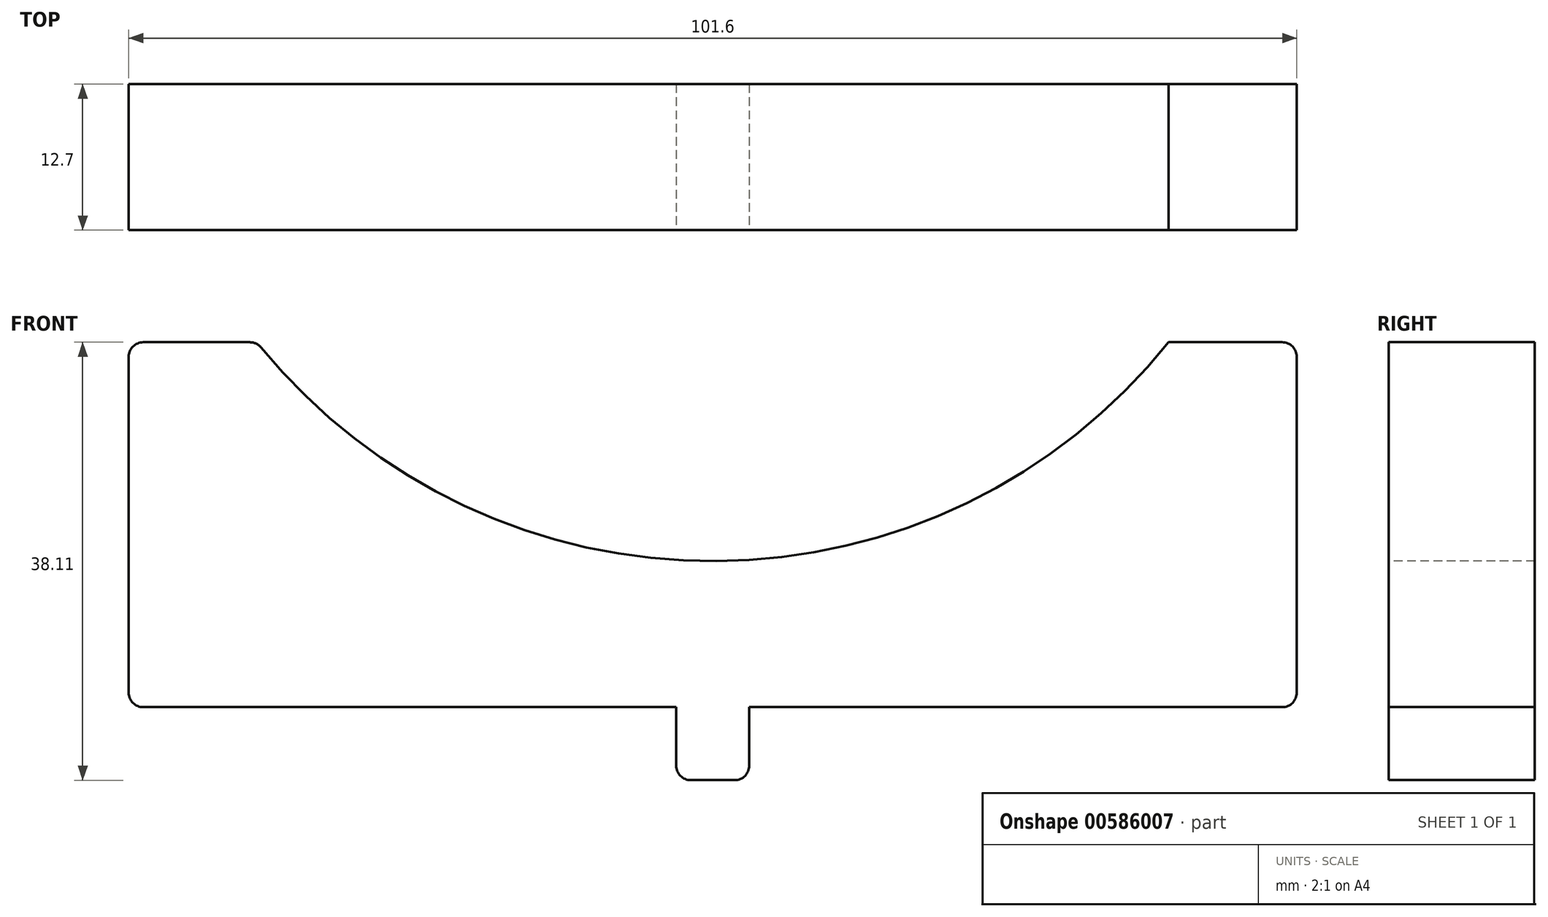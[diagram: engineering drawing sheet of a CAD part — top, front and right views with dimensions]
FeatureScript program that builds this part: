
annotation { "Feature Type Name" : "Feature", "Feature Type Description" : "" }
export const myFeature = defineFeature(function(context is Context, id is Id, definition is map)
    precondition{}
    {
        {
            var Q0;
            Q0=qCreatedBy(makeId("Front.planeOp"),FACE);
            var sketch = newSketch(context, id + "F0", { "sketchPlane" : qUnion([Q0])});
            skLineSegment(sketch, "E0.bottom", {"start": v(50.8, -15.87) * mm, "end": v(-50.8, -15.88) * mm});
            skLineSegment(sketch, "E0.top", {"start": v(50.8, 15.88) * mm, "end": v(-50.8, 15.87) * mm});
            skLineSegment(sketch, "E0.left", {"start": v(50.8, -15.88) * mm, "end": v(50.8, 15.88) * mm});
            skLineSegment(sketch, "E0.right", {"start": v(-50.8, -15.88) * mm, "end": v(-50.8, 15.87) * mm});
            skPoint(sketch, "E0.middle", {"position": v(0, 0) * mm});
            skSolve(sketch);
        }
        {
            var Q0;
            Q0=makeQuery(id+"F0.imprint","IMPRINT",FACE,{"disambiguationData":[TD([[makeQuery(id+"F0.imprint","IMPRINT",EDGE,{"derivedFrom":sQuery(id+"F0.wireOp",EDGE,"E0.bottom")}),-1.0]])]});
            extrude(context, id + "F1", {"entities" : qUnion([Q0]), "endBound" : BoundingType.SYMMETRIC, "depth" : 12.7 * mm, "offsetDistance" : 25.4 * mm});
        }
        {
            var Q0;
            Q0=qCreatedBy(makeId("Front.planeOp"),FACE);
            var sketch = newSketch(context, id + "F2", { "sketchPlane" : qUnion([Q0])});
            skArc(sketch, "E1", {"start": v(-39.66, 15.87) * mm, "mid": v(0, -3.17) * mm, "end": v(39.66, 15.87) * mm});
            skLineSegment(sketch, "E2", {"start": v(-39.66, 15.87) * mm, "end": v(39.66, 15.88) * mm});
            skSolve(sketch);
        }
        {
            var Q0;
            Q0 = qSketchRegion(id + "F2", true);
            extrude(context, id + "F3", {"entities" : qUnion([Q0]), "operationType" : NewBodyOperationType.REMOVE, "endBound" : BoundingType.SYMMETRIC, "oppositeDirection" : true, "depth" : 25.4 * mm, "offsetDistance" : 25.4 * mm});
        }
        {
            var Q0;
            Q0=makeQuery(id+"F1.opExtrude","SWEPT_FACE",FACE,{"disambiguationData":[OSD([sQuery(id+"F0.wireOp",EDGE,"E0.bottom")])]});
            var sketch = newSketch(context, id + "F4", { "sketchPlane" : qUnion([Q0])});
            skLineSegment(sketch, "E3.bottom", {"start": v(3.18, -6.35) * mm, "end": v(-3.18, -6.35) * mm});
            skLineSegment(sketch, "E3.top", {"start": v(3.18, 6.35) * mm, "end": v(-3.18, 6.35) * mm});
            skLineSegment(sketch, "E3.left", {"start": v(3.18, -6.35) * mm, "end": v(3.18, 6.35) * mm});
            skLineSegment(sketch, "E3.right", {"start": v(-3.18, -6.35) * mm, "end": v(-3.18, 6.35) * mm});
            skPoint(sketch, "E3.middle", {"position": v(0, 0) * mm});
            skSolve(sketch);
        }
        {
            var Q0;
            Q0=makeQuery(id+"F4.imprint","IMPRINT",FACE,{"disambiguationData":[TD([[makeQuery(id+"F4.imprint","IMPRINT",EDGE,{"derivedFrom":sQuery(id+"F4.wireOp",EDGE,"E3.bottom")}),-1.0]])]});
            extrude(context, id + "F5", {"entities" : qUnion([Q0]), "operationType" : NewBodyOperationType.ADD, "depth" : 6.35 * mm, "offsetDistance" : 25.4 * mm});
        }
        {
            var Q0;
            Q0=makeQuery(id+"F5.opExtrude","CAP_EDGE",EDGE,{"disambiguationData":[OSD([sQuery(id+"F4.wireOp",EDGE,"E3.right")])],"isStart":false});
            var Q1;
            Q1=makeQuery(id+"F5.opExtrude","CAP_EDGE",EDGE,{"disambiguationData":[OSD([sQuery(id+"F4.wireOp",EDGE,"E3.left")])],"isStart":false});
            var Q2;
            Q2=makeQuery(id+"F1.opExtrude","SWEPT_EDGE",EDGE,{"disambiguationData":[OSD([sQuery(id+"F0.wireOp",EDGE,"E0.bottom"),sQuery(id+"F0.wireOp",EDGE,"E0.right")])]});
            var Q3;
            Q3=makeQuery(id+"F1.opExtrude","SWEPT_EDGE",EDGE,{"disambiguationData":[OSD([sQuery(id+"F0.wireOp",EDGE,"E0.top"),sQuery(id+"F0.wireOp",EDGE,"E0.right")])]});
            var Q4;
            {var subQ0=sQuery(id+"F2.wireOp",EDGE,"E2");var subQ1=sQuery(id+"F2.wireOp",EDGE,"E1");Q4=makeQuery(id+"F3.boolean.opBoolean","COPY",EDGE,{"derivedFrom":makeQuery(id+"F3.opExtrude","SWEPT_EDGE",EDGE,{"disambiguationData":[OSD([subQ1,subQ0]),TDD([makeQuery(id+"F2.imprint","INTERSECT",VERTEX,{"disambiguationData":[OD(0.0)],"derivedFrom":[subQ1,subQ0]})])]})});}
            var Q5;
            {var subQ0=sQuery(id+"F2.wireOp",EDGE,"E2");var subQ1=sQuery(id+"F2.wireOp",EDGE,"E1");Q5=makeQuery(id+"F3.boolean.opBoolean","COPY",EDGE,{"derivedFrom":makeQuery(id+"F3.opExtrude","SWEPT_EDGE",EDGE,{"disambiguationData":[OSD([subQ1,subQ0]),TDD([makeQuery(id+"F2.imprint","INTERSECT",VERTEX,{"disambiguationData":[OD(1.0)],"derivedFrom":[subQ1,subQ0]})])]})});}
            var Q6;
            Q6=makeQuery(id+"F1.opExtrude","SWEPT_EDGE",EDGE,{"disambiguationData":[OSD([sQuery(id+"F0.wireOp",EDGE,"E0.top"),sQuery(id+"F0.wireOp",EDGE,"E0.left")])]});
            var Q7;
            Q7=makeQuery(id+"F1.opExtrude","SWEPT_EDGE",EDGE,{"disambiguationData":[OSD([sQuery(id+"F0.wireOp",EDGE,"E0.bottom"),sQuery(id+"F0.wireOp",EDGE,"E0.left")])]});
            fillet(context, id + "F6", {"entities" : qUnion([Q0, Q1, Q2, Q3, Q4, Q5, Q6, Q7]), "radius" : 1.27 * mm, "tangentPropagation" : true, "allowEdgeOverflow" : false});
        }
    });
